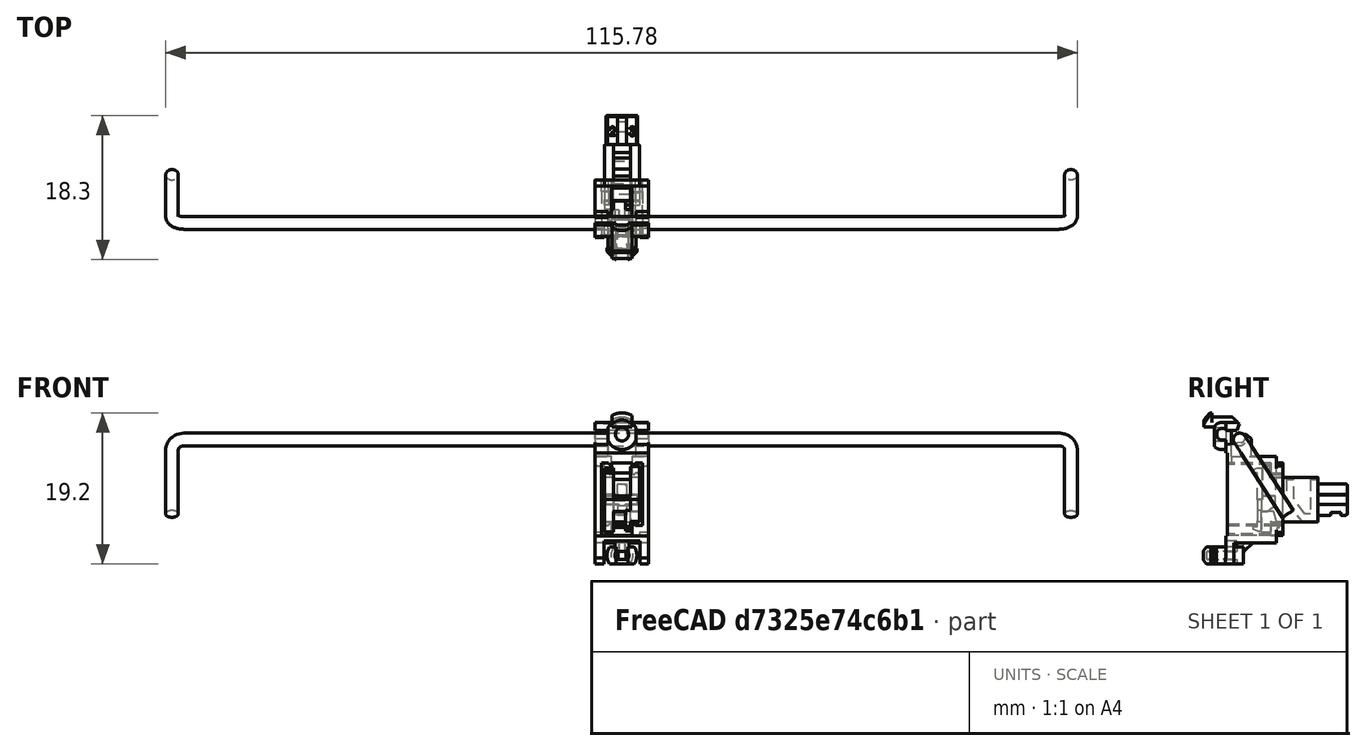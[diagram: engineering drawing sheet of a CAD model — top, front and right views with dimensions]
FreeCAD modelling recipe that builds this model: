
FCSTD DOCUMENT  (FreeCAD 0.18R16158 (Git))
Label: Stabilizer_Cherry_MX_7u
License: CreativeCommons Attribution-ShareAlike
LicenseURL: http://creativecommons.org/licenses/by-sa/4.0/
objects: Part::Feature×4, App::Part×3, PartDesign::Plane×2, Sketcher::SketchObject×2, PartDesign::AdditivePipe×1, PartDesign::Body×1
note: 11 computed .brp shape members not serialized (recipe doc carries the construction recipe); baked Part::Feature solids carry a one-line shape summary decoded from their .brp

FEATURE [Part::Feature] Part__Feature  label="Stabilizer_Base"
  shape: bbox 6.802 x 10.1 x 19.67 mm, 163 faces (baked)
FEATURE [Part::Feature] Part__Feature001  label="Stabilizer_Key"
  Placement = pos=(0,8.1,0) rot=(0,0,1;0rad)
  shape: bbox 4.6 x 11.96 x 8.302 mm, 299 faces (baked)
FEATURE [App::Part] Part  label="Stabilizer_End_1"
  Group = -> [Part__Feature001,Part__Feature]
  Origin = -> Origin001
  Placement = pos=(-57.15,0,0) rot=(0,0,1;0rad)
FEATURE [PartDesign::Plane] DatumPlane
  Length = 127.088
  MapMode = 13
  Placement = pos=(23.0333,0.289849,4.3056) rot=(1,0,0;2.14498rad)
  ResizeMode = 0
  Width = 38.9725
FEATURE [PartDesign::Plane] DatumPlane001
  Length = 38.9725
  MapMode = 11
  Placement = pos=(8e-15,4.09188,-1.57187) rot=(0.272451,-0.272451,0.92279;1.65106rad)
  ResizeMode = 0
  Width = 127.088
FEATURE [Sketcher::SketchObject] Sketch
  MapMode = 5
  Placement = pos=(8e-15,4.09188,-1.57187) rot=(0.272451,-0.272451,0.92279;1.65106rad)
  Support = -> [DatumPlane001]
  sketch-geometry (5):
    g0: Circle CenterX=0 CenterY=57.15 CenterZ=0 NormalX=0 NormalY=0 NormalZ=1 AngleXU=0 Radius=0.8
    g1: Circle [constr] CenterX=0 CenterY=-57.15 CenterZ=0 NormalX=0 NormalY=0 NormalZ=1 AngleXU=0 Radius=0.8
    g2: LineSegment [constr] StartX=0 StartY=57.15 StartZ=0 EndX=0 EndY=0 EndZ=0
    g3: LineSegment [constr] StartX=0 StartY=0 StartZ=0 EndX=0 EndY=-57.15 EndZ=0
    g4: GeomPoint X=0 Y=-57.15 Z=0
  constraints (11):
    c: Diameter(g0) = 1.6
    c: PointOnObject(g0,g-2)
    c: PointOnObject(g1,g-2)
    c: Coincident(g2,g0)
    c: Coincident(g2,g-1)
    c: Coincident(g3,g-1)
    c: Coincident(g3,g1)
    c: Equal(g3,g2)
    c: Distance(g2) = 57.15
    c: Equal(g1,g0)
    c: Coincident(g4,g1)
FEATURE [Sketcher::SketchObject] Sketch001
  ExternalGeometry = -> [Sketch]
  MapMode = 5
  Placement = pos=(23.0333,0.289849,4.3056) rot=(1,0,0;2.14498rad)
  Support = -> [DatumPlane]
  sketch-geometry (5):
    g0: LineSegment StartX=-79.442 StartY=-7.30074 StartZ=0 EndX=-79.442 EndY=2.42926 EndZ=0
    g1: LineSegment StartX=-78.642 StartY=3.22926 StartZ=0 EndX=32.458 EndY=3.22926 EndZ=0
    g2: LineSegment StartX=33.258 StartY=2.42926 StartZ=0 EndX=33.258 EndY=-7.30074 EndZ=0
    g3: ArcOfCircle CenterX=-78.642 CenterY=2.42926 CenterZ=0 NormalX=0 NormalY=0 NormalZ=1 AngleXU=0 Radius=0.8 StartAngle=1.5708 EndAngle=3.14159
    g4: ArcOfCircle CenterX=32.458 CenterY=2.42926 CenterZ=0 NormalX=0 NormalY=0 NormalZ=1 AngleXU=0 Radius=0.8 StartAngle=0 EndAngle=1.5708
FEATURE [PartDesign::AdditivePipe] AdditivePipe
  AuxilleryCurvelinear = true
  AuxillerySpineTangent = false
  Binormal = (0,0,0)
  Mode = 0
  Placement = pos=(8e-15,4.09188,-1.57187) rot=(0.272451,-0.272451,0.92279;1.65106rad)
  Profile = -> Sketch
  Spine = -> Sketch001
  SpineTangent = false
  Transformation = 0
  Transition = 0
FEATURE [PartDesign::Body] Body  label="Bar"
  Group = -> [DatumPlane,DatumPlane001,Sketch,Sketch001,AdditivePipe]
  Origin = -> Origin002
  Tip = -> AdditivePipe
FEATURE [Part::Feature] Part__Feature002  label="Stabilizer_Key_"
  Placement = pos=(0,8.1,0) rot=(0,0,1;0rad)
  shape: bbox 4.6 x 11.96 x 8.302 mm, 299 faces (baked)
FEATURE [Part::Feature] Part__Feature003  label="Stabilizer_Base_"
  shape: bbox 6.802 x 10.1 x 19.67 mm, 163 faces (baked)
FEATURE [App::Part] Part001  label="Stabilizer_End_2"
  Group = -> [Part__Feature002,Part__Feature003]
  Origin = -> Origin003
  Placement = pos=(57.145,0,0) rot=(0,0,1;0rad)
FEATURE [App::Part] Stabilizer___open  label="Stabilizer_Cherry_MX_7u"
  Group = -> [Body,Part001,Part]
  Origin = -> Origin
  Placement = pos=(0,8e-16,3.65) rot=(1,0,0;1.5708rad)
